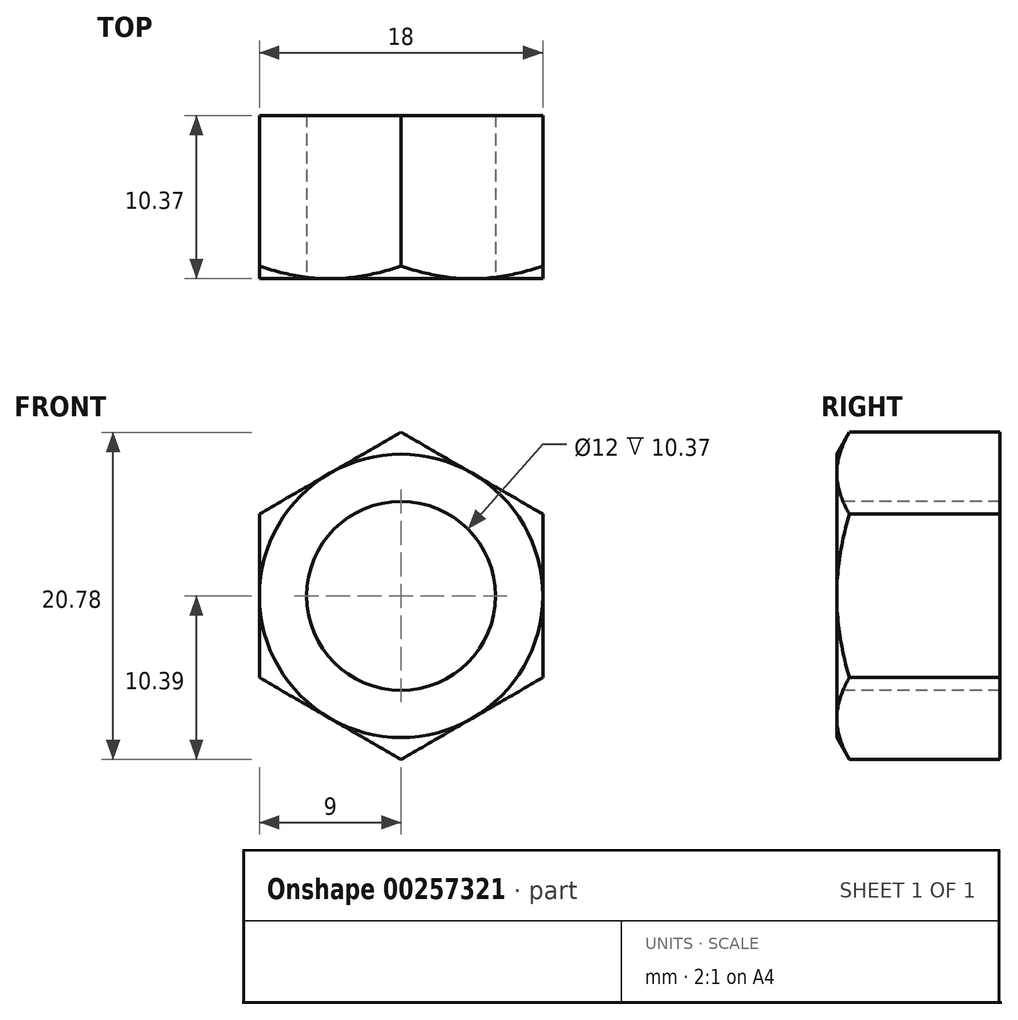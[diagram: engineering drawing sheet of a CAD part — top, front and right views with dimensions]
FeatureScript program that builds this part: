
annotation { "Feature Type Name" : "Feature", "Feature Type Description" : "" }
export const myFeature = defineFeature(function(context is Context, id is Id, definition is map)
    precondition{}
    {
        {
            var Q0;
            Q0=qCreatedBy(makeId("Front.planeOp"),FACE);
            var sketch = newSketch(context, id + "F0", { "sketchPlane" : qUnion([Q0])});
            skCircle(sketch, "E0.cCircle", {"center": v(0, 0) * mm, "radius": 9 * mm, "construction": true});
            skLineSegment(sketch, "E0.0", {"start": v(9, 5.2) * mm, "end": v(9, -5.2) * mm});
            skLineSegment(sketch, "E0.1", {"start": v(9, -5.2) * mm, "end": v(0, -10.4) * mm});
            skLineSegment(sketch, "E0.2", {"start": v(0, -10.4) * mm, "end": v(-9, -5.2) * mm});
            skLineSegment(sketch, "E0.3", {"start": v(-9, -5.2) * mm, "end": v(-9, 5.2) * mm});
            skLineSegment(sketch, "E0.4", {"start": v(-9, 5.2) * mm, "end": v(0, 10.4) * mm});
            skLineSegment(sketch, "E0.5", {"start": v(0, 10.4) * mm, "end": v(9, 5.2) * mm});
            skPoint(sketch, "E0.0.midPoint", {"position": v(9, 0) * mm});
            skSolve(sketch);
        }
        {
            var Q0;
            Q0=makeQuery(id+"F0.imprint","IMPRINT",FACE,{"disambiguationData":[TD([[makeQuery(id+"F0.imprint","IMPRINT",EDGE,{"derivedFrom":sQuery(id+"F0.wireOp",EDGE,"E0.0")}),-1.0]])]});
            extrude(context, id + "F1", {"entities" : qUnion([Q0]), "oppositeDirection" : true, "depth" : 10.37 * mm});
        }
        {
            var Q0;
            Q0=qCreatedBy(makeId("Right.planeOp"),FACE);
            var sketch = newSketch(context, id + "F2", { "sketchPlane" : qUnion([Q0])});
            skLineSegment(sketch, "E1", {"start": v(0, 9) * mm, "end": v(3.11, 14.4) * mm});
            skLineSegment(sketch, "E2", {"start": v(3.11, 14.4) * mm, "end": v(0, 14.4) * mm});
            skLineSegment(sketch, "E3", {"start": v(0, 14.4) * mm, "end": v(0, 9) * mm});
            skLineSegment(sketch, "E4", {"start": v(-5.97, 0) * mm, "end": v(11.57, 0) * mm, "construction": true});
            skSolve(sketch);
        }
        {
            var Q0;
            Q0 = qSketchRegion(id + "F2", true);
            var Q1;
            Q1=sQuery(id+"F2.wireOp",EDGE,"E4");
            revolve(context, id + "F3", {"operationType" : NewBodyOperationType.REMOVE, "entities" : qUnion([Q0]), "axis" : qUnion([Q1]), "revolveType" : RevolveType.FULL, "oppositeDirection" : true});
        }
        {
            var Q0;
            Q0=makeQuery(id+"F1.opExtrude","CAP_FACE",FACE,{"disambiguationData":[OSD([sQuery(id+"F0.wireOp",EDGE,"E0.0"),sQuery(id+"F0.wireOp",EDGE,"E0.1"),sQuery(id+"F0.wireOp",EDGE,"E0.2"),sQuery(id+"F0.wireOp",EDGE,"E0.3"),sQuery(id+"F0.wireOp",EDGE,"E0.4"),sQuery(id+"F0.wireOp",EDGE,"E0.5")])],"isStart":true});
            var sketch = newSketch(context, id + "F4", { "sketchPlane" : qUnion([Q0])});
            skPoint(sketch, "E5", {"position": v(0, 0) * mm});
            skSolve(sketch);
        }
        {
            var Q0;
            Q0=sQuery(id+"F4.wireOp",VERTEX,"E5");
            var Q1;
            Q1=makeQuery(id+"F1.opExtrude","SWEPT_BODY",BODY,{"disambiguationData":[OSD([sQuery(id+"F0.wireOp",EDGE,"E0.0"),sQuery(id+"F0.wireOp",EDGE,"E0.1"),sQuery(id+"F0.wireOp",EDGE,"E0.2"),sQuery(id+"F0.wireOp",EDGE,"E0.3"),sQuery(id+"F0.wireOp",EDGE,"E0.4"),sQuery(id+"F0.wireOp",EDGE,"E0.5")])]});
            hole(context, id + "F5", {"style" : HoleStyle.SIMPLE, "endStyle" : HoleEndStyle.THROUGH, "holeDiameter" : 12 * mm, "tappedDepth" : 12 * mm, "tapClearance" : 3, "locations" : qUnion([Q0]), "scope" : qUnion([Q1])});
        }
    });
